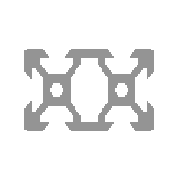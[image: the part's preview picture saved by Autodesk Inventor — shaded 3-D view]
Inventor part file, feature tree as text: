
AUTODESK INVENTOR PART (.ipt)
format: ipt  version: 2013 SP2 (Build 170200200, 200)  size: 195,072 bytes
history: native  units: mm
features: other x3, sketch x3, plane x1
ambient origin geometry x8: Origin, YZ Plane, XZ Plane, XY Plane, X Axis, Y Axis, Z Axis, Center Point
bodies: Solid1 (feature_tree), Body (feature_tree)
feature tree (7):
  other  "Driven Length"
  other  "Start Plane"
  other  "End Plane"
  sketch  "Sketch3"  dims[d2=10.0mm]
  sketch  "Sketch4"  dims[d26=10.0mm]
  plane  "Work Plane3"
  sketch  "Sketch5"  dims[d27=10.0mm d28=4.2mm d29=1.5mm d30=45.0deg d32=45.0deg d33=1.64mm d34=1.8mm d35=10.0mm d36=5.68mm d37=30.0mm d39=180.0deg d41=1.96mm d42=5.68mm d45=1.8mm d46=-0.0mm d47=10.0mm d48=0.13mm d49=0.0mm d50=90.0deg d51=10.0mm]
